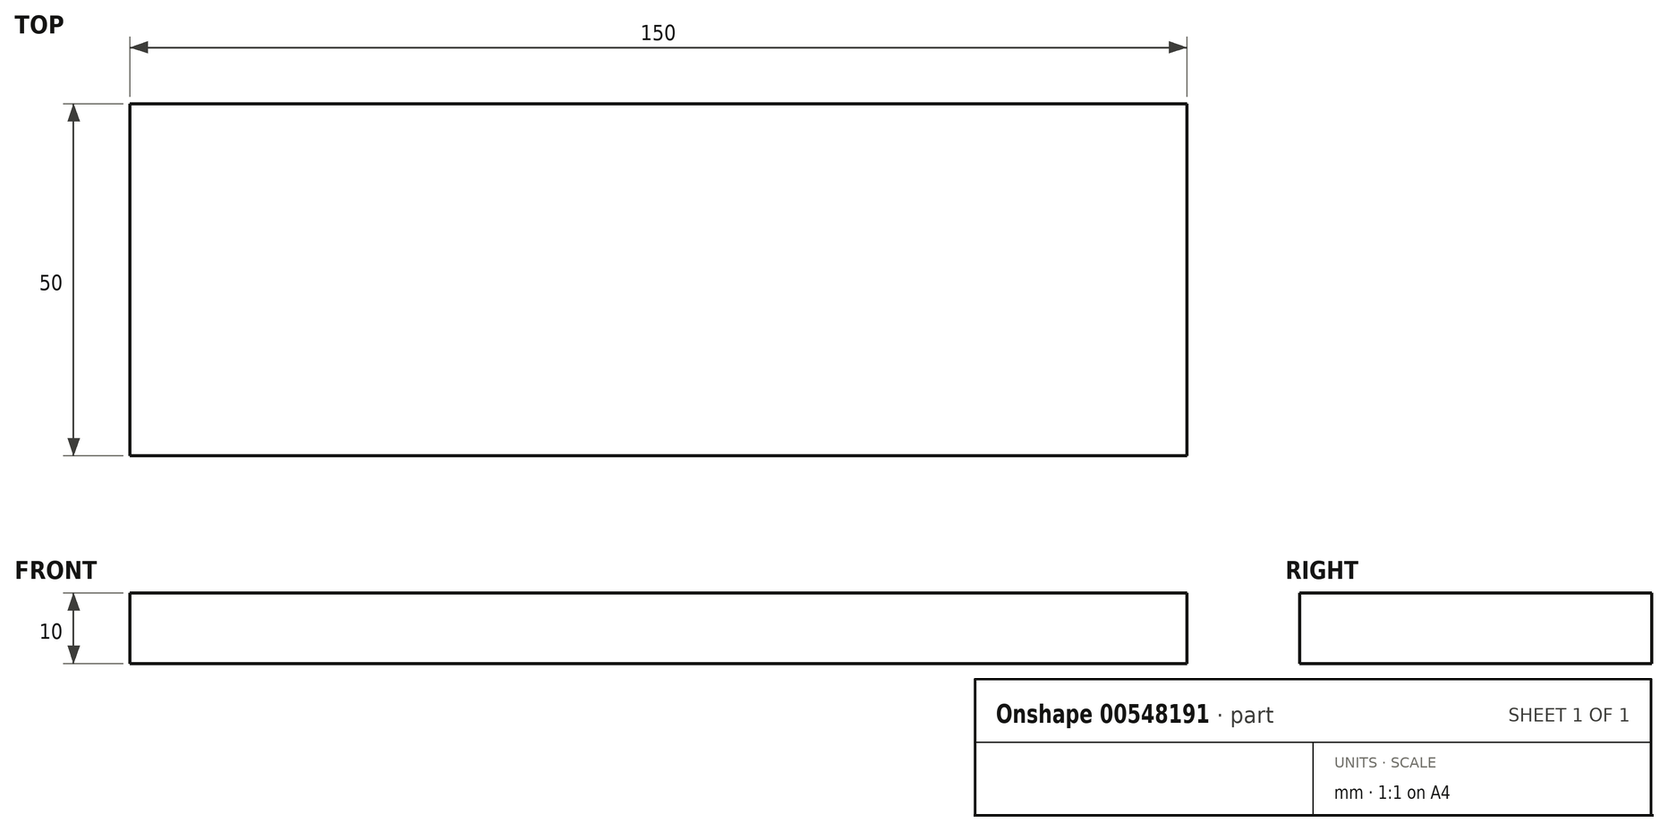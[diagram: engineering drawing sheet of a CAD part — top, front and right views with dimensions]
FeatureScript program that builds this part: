
annotation { "Feature Type Name" : "Feature", "Feature Type Description" : "" }
export const myFeature = defineFeature(function(context is Context, id is Id, definition is map)
    precondition{}
    {
        {
            var Q0;
            Q0=qCreatedBy(makeId("Top.planeOp"),FACE);
            var sketch = newSketch(context, id + "F0", { "sketchPlane" : qUnion([Q0])});
            skLineSegment(sketch, "E0.bottom", {"start": v(0, 0) * mm, "end": v(150, 0) * mm});
            skLineSegment(sketch, "E0.top", {"start": v(0, 50) * mm, "end": v(150, 50) * mm});
            skLineSegment(sketch, "E0.left", {"start": v(0, 0) * mm, "end": v(0, 50) * mm});
            skLineSegment(sketch, "E0.right", {"start": v(150, 0) * mm, "end": v(150, 50) * mm});
            skSolve(sketch);
        }
        {
            var Q0;
            Q0=makeQuery(id+"F0.imprint","IMPRINT",FACE,{"disambiguationData":[TD([[makeQuery(id+"F0.imprint","IMPRINT",EDGE,{"derivedFrom":sQuery(id+"F0.wireOp",EDGE,"E0.bottom")}),1.0]])]});
            extrude(context, id + "F1", {"entities" : qUnion([Q0]), "depth" : 10 * mm, "offsetDistance" : 25 * mm});
        }
    });
